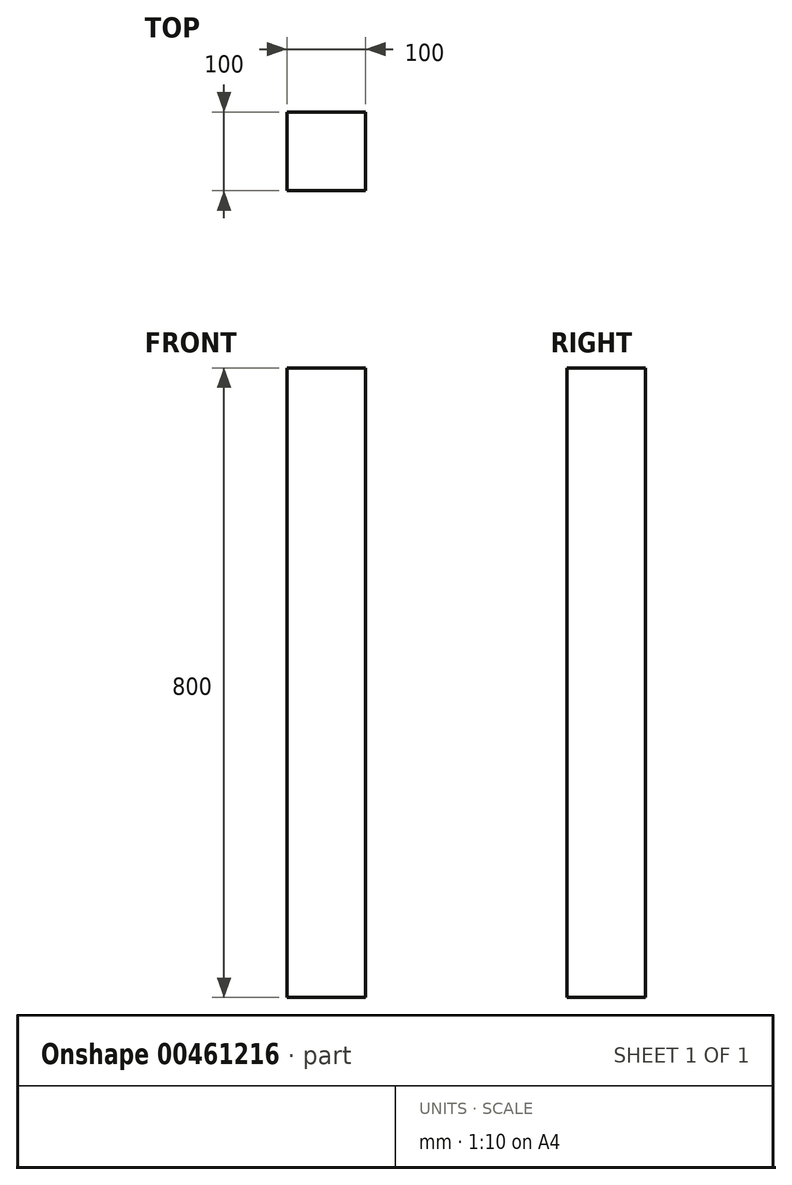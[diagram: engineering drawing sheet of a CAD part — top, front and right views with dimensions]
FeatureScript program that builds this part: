
annotation { "Feature Type Name" : "Feature", "Feature Type Description" : "" }
export const myFeature = defineFeature(function(context is Context, id is Id, definition is map)
    precondition{}
    {
        {
            var Q0;
            Q0=qCreatedBy(makeId("Top.planeOp"),FACE);
            var sketch = newSketch(context, id + "F0", { "sketchPlane" : qUnion([Q0])});
            skLineSegment(sketch, "E0.bottom", {"start": v(0, 0) * mm, "end": v(100, 0) * mm});
            skLineSegment(sketch, "E0.top", {"start": v(0, -100) * mm, "end": v(100, -100) * mm});
            skLineSegment(sketch, "E0.left", {"start": v(0, 0) * mm, "end": v(0, -100) * mm});
            skLineSegment(sketch, "E0.right", {"start": v(100, 0) * mm, "end": v(100, -100) * mm});
            skSolve(sketch);
        }
        {
            var Q0;
            Q0 = qSketchRegion(id + "F0", true);
            extrude(context, id + "F1", {"entities" : qUnion([Q0]), "depth" : 800 * mm});
        }
    });
